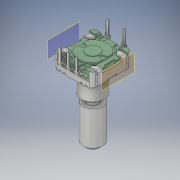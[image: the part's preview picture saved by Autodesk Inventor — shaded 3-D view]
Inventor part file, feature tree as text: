
AUTODESK INVENTOR PART (.ipt)
format: ipt  version: 2018 (Build 220112000, 112)  size: 655,872 bytes
history: native  units: mm
features: plane x2, extrude x2, sketch x2
ambient origin geometry x8: Origin, YZ Plane, XZ Plane, XY Plane, X Axis, Y Axis, Z Axis, Center Point
bodies: Volumenkörper1 (feature_tree)
feature tree (6):
  plane  "Arbeitsebene2"
  extrude  "Extrusion1"  Depth=2.17mm TaperAngle=0.0deg
  plane  "Arbeitsebene3"
  extrude  "Extrusion2"  Depth=3.43mm TaperAngle=0.0deg
  sketch  "Skizze1"  dims[d0=1.75mm d1=2.17mm d2=0.0mm]
  sketch  "Skizze2"  dims[d3=3.0mm d4=3.43mm d5=0.0mm]
